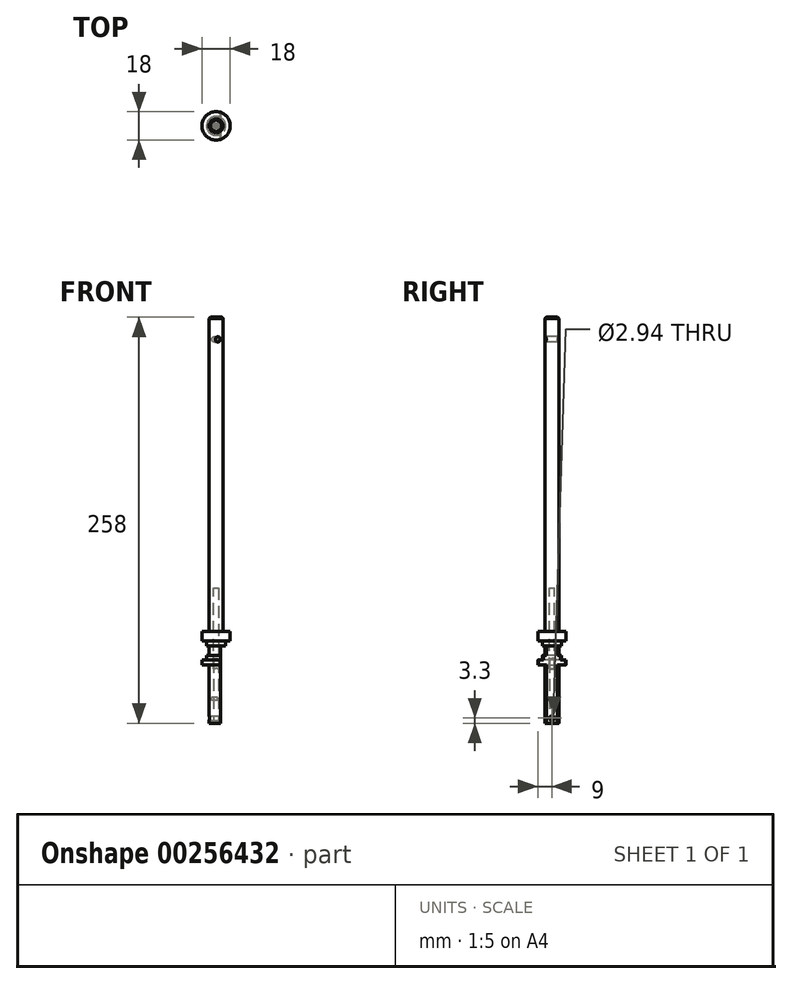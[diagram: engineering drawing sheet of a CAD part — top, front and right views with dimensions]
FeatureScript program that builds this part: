
annotation { "Feature Type Name" : "Feature", "Feature Type Description" : "" }
export const myFeature = defineFeature(function(context is Context, id is Id, definition is map)
    precondition{}
    {
        {
            var Q0;
            Q0=qCreatedBy(makeId("Top.planeOp"),FACE);
            var sketch = newSketch(context, id + "F0", { "sketchPlane" : qUnion([Q0])});
            skCircle(sketch, "E0", {"center": v(0, 0) * mm, "radius": 1.48 * mm});
            skSolve(sketch);
        }
        {
            var Q0;
            Q0=makeQuery(id+"F0.imprint","IMPRINT",FACE,{"disambiguationData":[TD([[makeQuery(id+"F0.imprint","IMPRINT",EDGE,{"derivedFrom":sQuery(id+"F0.wireOp",EDGE,"E0")}),1.0]])]});
            extrude(context, id + "F1", {"entities" : qUnion([Q0]), "depth" : 86 * mm});
        }
        {
            var Q0;
            Q0=makeQuery(id+"F1.opExtrude","CAP_EDGE",EDGE,{"disambiguationData":[OSD([sQuery(id+"F0.wireOp",EDGE,"E0")])],"isStart":false});
            chamfer(context, id + "F2", {"entities" : qUnion([Q0]), "width" : 0.3 * mm, "tangentPropagation" : true});
        }
        {
            var Q0;
            Q0=qCreatedBy(makeId("Front.planeOp"),FACE);
            var sketch = newSketch(context, id + "F3", { "sketchPlane" : qUnion([Q0])});
            skLineSegment(sketch, "E1", {"start": v(0, 0) * mm, "end": v(0, 86) * mm, "construction": true});
            skLineSegment(sketch, "E2", {"start": v(-3, 19.4) * mm, "end": v(0, 19.4) * mm});
            skLineSegment(sketch, "E3", {"start": v(-3, 19.4) * mm, "end": v(-3, 17.4) * mm});
            skLineSegment(sketch, "E4", {"start": v(-3, 17.4) * mm, "end": v(-2, 17.4) * mm});
            skLineSegment(sketch, "E5", {"start": v(-2, 13.4) * mm, "end": v(-3, 13.4) * mm});
            skLineSegment(sketch, "E6", {"start": v(-3, 13.4) * mm, "end": v(-3, 12.4) * mm});
            skLineSegment(sketch, "E7", {"start": v(-3, 12.4) * mm, "end": v(0, 12.4) * mm});
            skLineSegment(sketch, "E8", {"start": v(0, 19.4) * mm, "end": v(0, 12.4) * mm});
            skLineSegment(sketch, "E9", {"start": v(-2, 17.4) * mm, "end": v(-2, 16.4) * mm});
            skLineSegment(sketch, "E10", {"start": v(-2, 16.4) * mm, "end": v(0, 16.4) * mm});
            skLineSegment(sketch, "E11", {"start": v(0, 16.4) * mm, "end": v(0, 14.4) * mm});
            skLineSegment(sketch, "E12", {"start": v(0, 14.4) * mm, "end": v(-2, 14.4) * mm});
            skLineSegment(sketch, "E13", {"start": v(-2, 14.4) * mm, "end": v(-2, 13.4) * mm});
            skSolve(sketch);
        }
        {
            var Q0;
            {var subQ2=sQuery(id+"F3.wireOp",EDGE,"E2");Q0=makeQuery(id+"F3.imprint","IMPRINT",FACE,{"disambiguationData":[TD([[makeQuery(id+"F3.imprint","IMPRINT",EDGE,{"derivedFrom":subQ2}),-1.0]])]});}
            var Q1;
            Q1=makeQuery(id+"F3.imprint","IMPRINT",FACE,{"disambiguationData":[TD([[makeQuery(id+"F3.imprint","IMPRINT",EDGE,{"derivedFrom":sQuery(id+"F3.wireOp",EDGE,"E5")}),1.0]])]});
            var Q2;
            Q2=sQuery(id+"F3.wireOp",EDGE,"E8");
            revolve(context, id + "F4", {"operationType" : NewBodyOperationType.ADD, "entities" : qUnion([Q0, Q1]), "axis" : qUnion([Q2]), "revolveType" : RevolveType.FULL});
        }
        {
            var Q0;
            Q0=qCreatedBy(makeId("Right.planeOp"),FACE);
            var sketch = newSketch(context, id + "F5", { "sketchPlane" : qUnion([Q0])});
            skLineSegment(sketch, "E14", {"start": v(3, 16.4) * mm, "end": v(0, 16.4) * mm});
            skLineSegment(sketch, "E15", {"start": v(3, 16.4) * mm, "end": v(3, 14.4) * mm});
            skLineSegment(sketch, "E16", {"start": v(0, 14.4) * mm, "end": v(3, 14.4) * mm});
            skLineSegment(sketch, "E17", {"start": v(0, 14.4) * mm, "end": v(0, 16.4) * mm});
            skSolve(sketch);
        }
        {
            var Q0;
            Q0=makeQuery(id+"F5.imprint","IMPRINT",FACE,{"disambiguationData":[TD([[makeQuery(id+"F5.imprint","IMPRINT",EDGE,{"derivedFrom":sQuery(id+"F5.wireOp",EDGE,"E14")}),1.0]])]});
            var Q1;
            Q1=sQuery(id+"F3.wireOp",EDGE,"E8");
            revolve(context, id + "F6", {"entities" : qUnion([Q0]), "axis" : qUnion([Q1]), "revolveType" : RevolveType.SYMMETRIC, "angle" : 360 * degree});
        }
        {
            var Q0;
            Q0=makeQuery(id+"F6.opRevolve","SWEPT_FACE",FACE,{"disambiguationData":[OSD([sQuery(id+"F5.wireOp",EDGE,"E14")])]});
            var sketch = newSketch(context, id + "F7", { "sketchPlane" : qUnion([Q0]), "disableImprinting" : false});
            skLineSegment(sketch, "E18", {"start": v(0.9, 2.86) * mm, "end": v(0.9, -2.86) * mm});
            skSolve(sketch);
        }
        {
            var Q0;
            {var subQ1=sQuery(id+"F7.wireOp",EDGE,"E18");Q0=makeQuery(id+"F7.imprint","IMPRINT",FACE,{"disambiguationData":[TD([[makeQuery(id+"F7.imprint","IMPRINT",EDGE,{"derivedFrom":subQ1}),1.0]])]});}
            extrude(context, id + "F8", {"entities" : qUnion([Q0]), "operationType" : NewBodyOperationType.REMOVE, "endBound" : BoundingType.THROUGH_ALL, "oppositeDirection" : true, "depth" : 25 * mm});
        }
        {
            var Q0;
            Q0=makeQuery(id+"F1.opExtrude","CAP_FACE",FACE,{"disambiguationData":[OSD([sQuery(id+"F0.wireOp",EDGE,"E0")])],"isStart":false});
            cPlane(context, id + "F9", {"entities" : qUnion([Q0]), "cplaneType" : CPlaneType.OFFSET, "offset" : 4.7 * mm, "oppositeDirection" : true, "width" : 150 * mm, "height" : 150 * mm});
        }
        {
            var Q0;
            Q0=qCreatedBy(id+"F9.planeOp",FACE);
            var sketch = newSketch(context, id + "F10", { "sketchPlane" : qUnion([Q0])});
            skLineSegment(sketch, "E19", {"start": v(-0.23, 3) * mm, "end": v(1.3, -2.7) * mm});
            skLineSegment(sketch, "E20", {"start": v(-0.78, 2.9) * mm, "end": v(0.78, -2.9) * mm});
            skArc(sketch, "E21", {"start": v(0.78, -2.9) * mm, "mid": v(1.04, -2.81) * mm, "end": v(1.3, -2.7) * mm});
            skArc(sketch, "E22.trimOffspring", {"start": v(-0.23, 3) * mm, "mid": v(-0.5, 2.96) * mm, "end": v(-0.78, 2.9) * mm});
            skSolve(sketch);
        }
        {
            var Q0;
            Q0=makeQuery(id+"F10.imprint","IMPRINT",FACE,{"disambiguationData":[TD([[makeQuery(id+"F10.imprint","IMPRINT",EDGE,{"derivedFrom":sQuery(id+"F10.wireOp",EDGE,"E19")}),-1.0]])]});
            var Q1;
            Q1=sQuery(id+"F10.wireOp",EDGE,"E20");
            revolve(context, id + "F11", {"operationType" : NewBodyOperationType.REMOVE, "entities" : qUnion([Q0]), "axis" : qUnion([Q1]), "revolveType" : RevolveType.FULL, "oppositeDirection" : true});
        }
        {
            var Q0;
            Q0=qCreatedBy(makeId("Top.planeOp"),FACE);
            cPlane(context, id + "F12", {"entities" : qUnion([Q0]), "cplaneType" : CPlaneType.OFFSET, "offset" : 1.1 * mm, "width" : 150 * mm, "height" : 150 * mm});
        }
        {
            var Q0;
            Q0=qCreatedBy(id+"F12.planeOp",FACE);
            var sketch = newSketch(context, id + "F13", { "sketchPlane" : qUnion([Q0])});
            skLineSegment(sketch, "E23", {"start": v(-3, 0) * mm, "end": v(3, 0) * mm});
            skLineSegment(sketch, "E24", {"start": v(2.96, 0.5) * mm, "end": v(-2.96, 0.49) * mm});
            skArc(sketch, "E25", {"start": v(-2.96, 0.49) * mm, "mid": v(-2.99, 0.25) * mm, "end": v(-3, 0) * mm});
            skArc(sketch, "E26.trimOffspring", {"start": v(3, 0) * mm, "mid": v(2.99, 0.25) * mm, "end": v(2.96, 0.5) * mm});
            skSolve(sketch);
        }
        {
            var Q0;
            Q0=makeQuery(id+"F13.imprint","IMPRINT",FACE,{"disambiguationData":[TD([[makeQuery(id+"F13.imprint","IMPRINT",EDGE,{"derivedFrom":sQuery(id+"F13.wireOp",EDGE,"E23")}),1.0]])]});
            var Q1;
            Q1=sQuery(id+"F13.wireOp",EDGE,"E23");
            revolve(context, id + "F14", {"operationType" : NewBodyOperationType.REMOVE, "entities" : qUnion([Q0]), "axis" : qUnion([Q1]), "revolveType" : RevolveType.FULL, "oppositeDirection" : true});
        }
        {
            var Q0;
            Q0=qCreatedBy(makeId("Front.planeOp"),FACE);
            var sketch = newSketch(context, id + "F15", { "sketchPlane" : qUnion([Q0])});
            skLineSegment(sketch, "E27", {"start": v(-1.5, 34.45) * mm, "end": v(-1.5, 86) * mm});
            skLineSegment(sketch, "E28", {"start": v(-1.5, 86) * mm, "end": v(1.5, 86) * mm});
            skLineSegment(sketch, "E29", {"start": v(1.5, 86) * mm, "end": v(1.5, 34.45) * mm});
            skLineSegment(sketch, "E30", {"start": v(1.5, 34.45) * mm, "end": v(0.5, 34.45) * mm});
            skLineSegment(sketch, "E31", {"start": v(0.5, 34.45) * mm, "end": v(0.5, 34.85) * mm});
            skLineSegment(sketch, "E32", {"start": v(0.5, 34.85) * mm, "end": v(-0.5, 34.85) * mm});
            skLineSegment(sketch, "E33", {"start": v(-0.5, 34.85) * mm, "end": v(-0.5, 34.45) * mm});
            skLineSegment(sketch, "E34", {"start": v(-0.5, 34.45) * mm, "end": v(-1.5, 34.45) * mm});
            skSolve(sketch);
        }
        {
            var Q0;
            Q0=qSketchRegion(id+"F15",true);
            extrude(context, id + "F16", {"entities" : qUnion([Q0]), "depth" : 3 * mm, "symmetric" : true});
        }
        {
            var Q0;
            Q0=qCreatedBy(makeId("Right.planeOp"),FACE);
            var sketch = newSketch(context, id + "F17", { "sketchPlane" : qUnion([Q0])});
            skLineSegment(sketch, "E35", {"start": v(-1.57, 34.45) * mm, "end": v(-0.47, 34.45) * mm});
            skLineSegment(sketch, "E36", {"start": v(-0.48, 34.45) * mm, "end": v(-0.48, 34.85) * mm});
            skLineSegment(sketch, "E37", {"start": v(-0.48, 34.85) * mm, "end": v(0.48, 34.85) * mm});
            skLineSegment(sketch, "E38", {"start": v(0.48, 34.85) * mm, "end": v(0.48, 34.45) * mm});
            skLineSegment(sketch, "E39", {"start": v(0.47, 34.45) * mm, "end": v(1.57, 34.45) * mm});
            skLineSegment(sketch, "E40", {"start": v(1.58, 34.45) * mm, "end": v(6, 0) * mm});
            skLineSegment(sketch, "E41", {"start": v(6, 0) * mm, "end": v(-6, 0) * mm});
            skLineSegment(sketch, "E42", {"start": v(-6, 0) * mm, "end": v(-1.57, 34.45) * mm});
            skSolve(sketch);
        }
        {
            var Q0;
            Q0=makeQuery(id+"F1.opExtrude","SWEPT_BODY",BODY,{"disambiguationData":[OSD([sQuery(id+"F0.wireOp",EDGE,"E0")])]});
            var Q1;
            Q1=qCreatedBy(makeId("Origin.pointOp"),VERTEX);
            transform(context, id + "F18", {"entities" : qUnion([Q0]), "transformType" : TransformType.SCALE_UNIFORMLY, "scale" : 3, "makeCopy" : false, "scalePoint" : qUnion([Q1])});
        }
        {
            var Q0;
            Q0=qCreatedBy(id+"F12.planeOp",FACE);
            var sketch = newSketch(context, id + "F19", { "sketchPlane" : qUnion([Q0])});
            skCircle(sketch, "E43", {"center": v(0, 0) * mm, "radius": 1.55 * mm});
            skSolve(sketch);
        }
        {
            var Q0;
            Q0=qSketchRegion(id+"F19",true);
            extrude(context, id + "F20", {"entities" : qUnion([Q0]), "depth" : 40 * mm});
        }
        {
            var Q0;
            Q0=makeQuery(id+"F20.opExtrude","CAP_EDGE",EDGE,{"disambiguationData":[OSD([sQuery(id+"F19.wireOp",EDGE,"E43")])],"isStart":false});
            var Q1;
            Q1=makeQuery(id+"F20.opExtrude","CAP_EDGE",EDGE,{"disambiguationData":[OSD([sQuery(id+"F19.wireOp",EDGE,"E43")])],"isStart":true});
            fillet(context, id + "F21", {"entities" : qUnion([Q0, Q1]), "radius" : 1.5 * mm, "tangentPropagation" : true, "rho" : 0.7, "crossSection" : FilletCrossSection.CONIC, "allowEdgeOverflow" : false});
        }
    });
